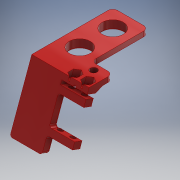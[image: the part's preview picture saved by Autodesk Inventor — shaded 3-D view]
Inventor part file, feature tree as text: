
AUTODESK INVENTOR PART (.ipt)
format: ipt  version: 2018.3 (Build 223284000, 284)  size: 548,352 bytes
history: native  units: mm
features: extrude x21, sketch x20, fillet x11, chamfer x3, projected_geometry x2, draft x1, plane x1
ambient origin geometry x8: Origin, YZ Plane, XZ Plane, XY Plane, X Axis, Y Axis, Z Axis, Center Point
bodies: Solid1 (feature_tree)
feature tree (59):
  extrude  "Extrusion1"  Depth=65.0mm
  sketch  "Sketch2"  dims[d2=4.0mm d3=0.0mm d4=16.5mm]
  extrude  "Extrusion5"  Depth=16.5mm
  extrude  "Extrusion8"  Depth=14.0mm
  fillet  "Fillet4"  Radius=14.0mm
  extrude  "Extrusion9"  Depth=4.0mm
  extrude  "Extrusion11"  Depth=4.0mm
  extrude  "Extrusion17"  TaperAngle=0.0deg  [1 undecoded]
  fillet  "Fillet10"  Radius=4.0mm
  extrude  "Extrusion20"  Depth=22.0mm
  extrude  "Extrusion21"  Depth=1.0mm
  extrude  "Extrusion23"  Depth=5.4mm
  extrude  "Extrusion25"  Depth=10.0mm TaperAngle=0.0deg
  extrude  "Extrusion29"  Depth=1.5mm
  extrude  "Extrusion30"  Depth=1.5mm
  extrude  "Extrusion31"  Depth=3.0mm TaperAngle=0.0deg
  fillet  "Fillet16"  Radius=0.5mm
  fillet  "Fillet18"  Radius=46.0mm
  extrude  "Extrusion32"  Depth=7.0mm
  chamfer  "Chamfer3"  Distance=25.0mm
  extrude  "Extrusion33"  Depth=25.0mm TaperAngle=0.0deg
  chamfer  "Chamfer4"  Distance=25.0mm
  fillet  "Fillet19"  Radius=1.5mm
  extrude  "Extrusion34"  Depth=5.0mm
  fillet  "Fillet20"  Radius=5.0mm
  draft  "FaceDraft1"
  chamfer  "Chamfer6"  Distance=3.0mm
  fillet  "Fillet21"  Radius=20.0mm
  extrude  "Extrusion35"  Depth=3.0mm TaperAngle=0.0deg
  extrude  "Extrusion42"  Depth=5.0mm
  fillet  "Fillet27"  Radius=29.0mm
  plane  "Work Plane6"
  sketch  "Sketch37"  dims[d141=1.0mm d142=0.0mm d161=5.0mm d165=5.0mm]
  extrude  "Extrusion43"  Depth=3.0mm TaperAngle=0.0deg
  extrude  "Extrusion44"  Depth=1.0mm
  extrude  "Extrusion45"  Depth=2.0mm
  fillet  "Fillet28"  Radius=19.5mm
  fillet  "Fillet29"  Radius=37.5mm
  fillet  "Fillet30"  Radius=7.5mm
  sketch  "Sketch1"  dims[d0=45.0mm d1=65.0mm]
  sketch  "Sketch4"  dims[d5=16.5mm d6=14.0mm d7=14.0mm]
  sketch  "Sketch6"  dims[d8=25.883mm d20=4.0mm]
  sketch  "Sketch8"  dims[d21=5.0mm d22=4.0mm]
  sketch  "Sketch13"  dims[d24=10.0mm d25=0.0mm d26=0.0mm d27=4.0mm]
  sketch  "Sketch16"  dims[d34=22.0mm d35=22.0mm]
  sketch  "Sketch17"  dims[d36=3.0mm d37=0.0mm d38=1.0mm]
  sketch  "Sketch19"  dims[d39=3.0mm d40=0.0mm d47=5.4mm]
  sketch  "Sketch20"  dims[d48=10.0mm d52=10.0mm d53=0.0mm]
  sketch  "Sketch23"  dims[d88=5.0mm d89=1.5mm]
  sketch  "Sketch24"  dims[d91=5.0mm d92=1.5mm]
  sketch  "Sketch25"  dims[d93=3.0mm d94=3.0mm d95=0.0mm d106=0.5mm d114=46.0mm]
  sketch  "Sketch26"  dims[d115=27.925268mm d116=7.0mm]
  sketch  "Sketch28"  dims[d117=19.198622mm]
  sketch  "Sketch29"  dims[d118=3.490659mm d119=25.0mm d120=0.0mm]
  sketch  "Sketch30"  dims[d123=3.490659mm d124=25.0mm d125=0.0mm]
  projected_geometry  "Projected Loop1"
  projected_geometry  "Projected Loop2"
  sketch  "Sketch36"  dims[d135=11.0mm d136=25.0mm d137=0.0mm d140=1.5mm]
  sketch  "Sketch38"  dims[d167=7.0mm d168=3.0mm d169=20.0mm d170=0.0mm d172=3.0mm d173=0.0mm d174=5.0mm d175=29.0mm d176=3.0mm d177=0.0mm d178=1.0mm d180=2.0mm d181=19.5mm d182=37.5mm d184=7.5mm d185=4.0mm d186=0.0mm d187=4.0mm d188=2.5mm d189=45.0deg d190=1.0mm d191=30.0mm d192=0.5mm d194=90.0deg d195=1.25mm d196=15.0mm d197=3.0mm d198=1.0mm d199=1.0mm d200=0.0mm d201=1.0mm d202=2.5mm d203=45.0deg d204=2.0mm d208=1.5mm d209=5.0mm d210=1.0mm d211=0.0mm d212=0.5mm d213=6.981317mm d214=2.5mm d215=4.5mm d216=30.0deg d217=2.0mm d218=1.0mm d219=0.0mm d242=15.0mm d260=17.0mm d261=45.0mm d262=10.0mm d263=0.0mm d264=4.0mm d265=-5.0mm d266=7.5mm d267=2.0mm d268=90.0deg d269=10.0mm d270=0.0mm d271=3.5mm d272=0.0mm d273=4.5mm d274=22.0mm d275=0.0mm d276=5.0mm d277=5.0mm d278=2.0mm]
note: 1 required parameter value undecoded (feature->parameter linkage not recoverable at this tier; creation-order binding heuristic only, values carry confidence <= 0.55)
